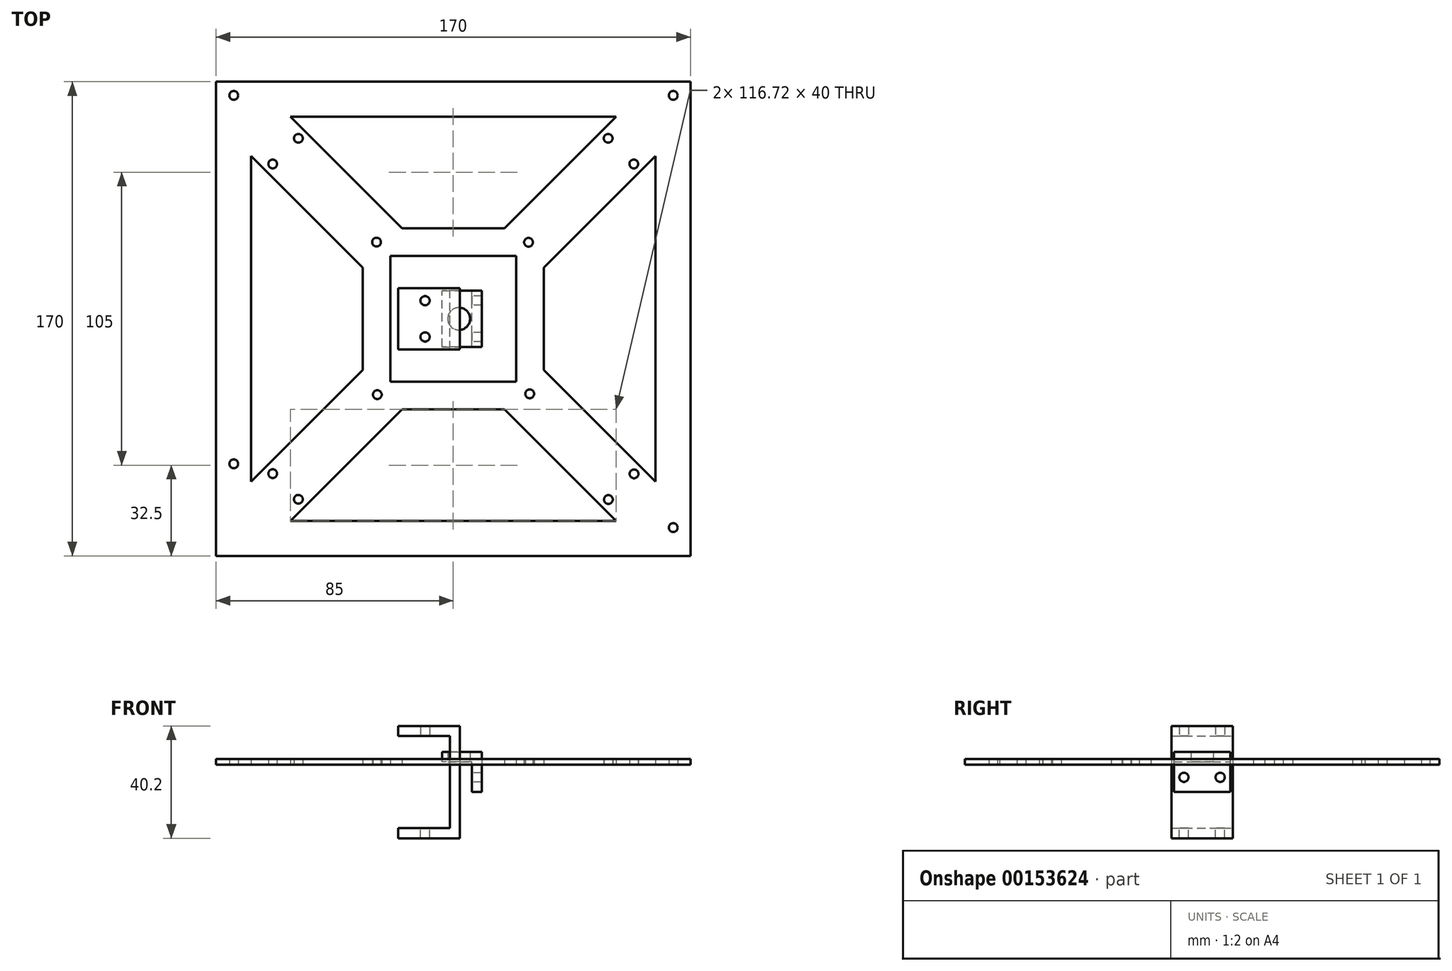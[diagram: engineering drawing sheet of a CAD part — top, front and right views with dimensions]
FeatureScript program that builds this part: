
annotation { "Feature Type Name" : "Feature", "Feature Type Description" : "" }
export const myFeature = defineFeature(function(context is Context, id is Id, definition is map)
    precondition{}
    {
        {
            var Q0;
            Q0=qCreatedBy(makeId("Front.planeOp"),FACE);
            var sketch = newSketch(context, id + "F0", { "sketchPlane" : qUnion([Q0])});
            skLineSegment(sketch, "E0", {"start": v(-19.76, 12.86) * mm, "end": v(2.4, 12.86) * mm});
            skLineSegment(sketch, "E1", {"start": v(2.4, 12.86) * mm, "end": v(2.4, -27.34) * mm});
            skLineSegment(sketch, "E2", {"start": v(2.4, -27.34) * mm, "end": v(-19.76, -27.34) * mm});
            skLineSegment(sketch, "E3", {"start": v(-19.76, -27.34) * mm, "end": v(-19.76, -23.74) * mm});
            skLineSegment(sketch, "E4", {"start": v(-19.76, -23.74) * mm, "end": v(-1.2, -23.74) * mm});
            skLineSegment(sketch, "E5", {"start": v(-1.2, -23.74) * mm, "end": v(-1.2, 9.26) * mm});
            skLineSegment(sketch, "E6", {"start": v(-1.2, 9.26) * mm, "end": v(-19.76, 9.26) * mm});
            skLineSegment(sketch, "E7", {"start": v(-19.76, 9.26) * mm, "end": v(-19.76, 12.86) * mm});
            skSolve(sketch);
        }
        {
            var Q0;
            Q0=makeQuery(id+"F0.imprint","IMPRINT",FACE,{"disambiguationData":[TD([[makeQuery(id+"F0.imprint","IMPRINT",EDGE,{"derivedFrom":sQuery(id+"F0.wireOp",EDGE,"E0")}),-1.0]])]});
            extrude(context, id + "F1", {"entities" : qUnion([Q0]), "endBound" : BoundingType.SYMMETRIC, "depth" : 22 * mm});
        }
        {
            var Q0;
            Q0=qCreatedBy(makeId("Top.planeOp"),FACE);
            var sketch = newSketch(context, id + "F2", { "sketchPlane" : qUnion([Q0])});
            skPoint(sketch, "E8", {"position": v(-10.1, 0) * mm});
            skPoint(sketch, "E9", {"position": v(-10.1, 6.5) * mm});
            skPoint(sketch, "E10", {"position": v(-10.1, -6.5) * mm});
            skSolve(sketch);
        }
        {
            var Q0;
            Q0=sQuery(id+"F2.wireOp",VERTEX,"E9");
            var Q1;
            Q1=sQuery(id+"F2.wireOp",VERTEX,"E10");
            var Q2;
            Q2=makeQuery(id+"F1.opExtrude","SWEPT_BODY",BODY,{"disambiguationData":[OSD([sQuery(id+"F0.wireOp",EDGE,"E0"),sQuery(id+"F0.wireOp",EDGE,"E1"),sQuery(id+"F0.wireOp",EDGE,"E2"),sQuery(id+"F0.wireOp",EDGE,"E3"),sQuery(id+"F0.wireOp",EDGE,"E4"),sQuery(id+"F0.wireOp",EDGE,"E5"),sQuery(id+"F0.wireOp",EDGE,"E6"),sQuery(id+"F0.wireOp",EDGE,"E7")])]});
            hole(context, id + "F3", {"style" : HoleStyle.SIMPLE, "endStyle" : HoleEndStyle.THROUGH, "standardTappedOrClearance" : lookupTablePath({ "standard" : "ISO", "fit" : "Normal", "size" : "M3", "type" : "Clearance" }), "standardBlindInLast" : lookupTablePath({ "fit" : "Standard", "standard" : "ISO", "size" : "M3", "type" : "Clearance" }), "holeDiameter" : 3.3 * mm, "locations" : qUnion([Q0, Q1]), "scope" : qUnion([Q2]), "isTappedThrough" : true});
        }
        {
            var Q0;
            Q0=sQuery(id+"F2.wireOp",VERTEX,"E10");
            var Q1;
            Q1=sQuery(id+"F2.wireOp",VERTEX,"E9");
            var Q2;
            Q2=makeQuery(id+"F1.opExtrude","SWEPT_BODY",BODY,{"disambiguationData":[OSD([sQuery(id+"F0.wireOp",EDGE,"E0"),sQuery(id+"F0.wireOp",EDGE,"E1"),sQuery(id+"F0.wireOp",EDGE,"E2"),sQuery(id+"F0.wireOp",EDGE,"E3"),sQuery(id+"F0.wireOp",EDGE,"E4"),sQuery(id+"F0.wireOp",EDGE,"E5"),sQuery(id+"F0.wireOp",EDGE,"E6"),sQuery(id+"F0.wireOp",EDGE,"E7")])]});
            hole(context, id + "F4", {"style" : HoleStyle.SIMPLE, "endStyle" : HoleEndStyle.THROUGH, "oppositeDirection" : true, "standardTappedOrClearance" : lookupTablePath({ "standard" : "ISO", "fit" : "Normal", "size" : "M3", "type" : "Clearance" }), "standardBlindInLast" : lookupTablePath({ "fit" : "Standard", "standard" : "ISO", "size" : "M3", "type" : "Clearance" }), "holeDiameter" : 3.3 * mm, "locations" : qUnion([Q0, Q1]), "scope" : qUnion([Q2]), "isTappedThrough" : true});
        }
        {
            var Q0;
            Q0=qCreatedBy(makeId("Front.planeOp"),FACE);
            var sketch = newSketch(context, id + "F5", { "sketchPlane" : qUnion([Q0])});
            skLineSegment(sketch, "E11", {"start": v(10.27, -10.7) * mm, "end": v(6.67, -10.7) * mm});
            skLineSegment(sketch, "E12", {"start": v(6.67, -10.7) * mm, "end": v(6.67, 0) * mm});
            skLineSegment(sketch, "E13", {"start": v(6.67, 0) * mm, "end": v(-4.03, 0) * mm});
            skLineSegment(sketch, "E14", {"start": v(-4.03, 0) * mm, "end": v(-4.03, 3.6) * mm});
            skLineSegment(sketch, "E15", {"start": v(-4.03, 3.6) * mm, "end": v(10.27, 3.6) * mm});
            skLineSegment(sketch, "E16", {"start": v(10.27, 3.6) * mm, "end": v(10.27, -10.7) * mm});
            skSolve(sketch);
        }
        {
            var Q0;
            Q0 = qSketchRegion(id + "F5", true);
            extrude(context, id + "F6", {"entities" : qUnion([Q0]), "endBound" : BoundingType.SYMMETRIC, "depth" : 20.2 * mm});
        }
        {
            var Q0;
            Q0=qCreatedBy(makeId("Right.planeOp"),FACE);
            var sketch = newSketch(context, id + "F7", { "sketchPlane" : qUnion([Q0])});
            skPoint(sketch, "E17", {"position": v(0, 0) * mm});
            skPoint(sketch, "E18", {"position": v(0, -5.5) * mm});
            skPoint(sketch, "E19", {"position": v(-6.5, -5.5) * mm});
            skPoint(sketch, "E20", {"position": v(6.5, -5.5) * mm});
            skSolve(sketch);
        }
        {
            var Q0;
            Q0=sQuery(id+"F7.wireOp",VERTEX,"E19");
            var Q1;
            Q1=sQuery(id+"F7.wireOp",VERTEX,"E20");
            var Q2;
            Q2=makeQuery(id+"F6.opExtrude","SWEPT_BODY",BODY,{"disambiguationData":[OSD([sQuery(id+"F5.wireOp",EDGE,"E11"),sQuery(id+"F5.wireOp",EDGE,"E12"),sQuery(id+"F5.wireOp",EDGE,"E13"),sQuery(id+"F5.wireOp",EDGE,"E14"),sQuery(id+"F5.wireOp",EDGE,"E15"),sQuery(id+"F5.wireOp",EDGE,"E16")])]});
            hole(context, id + "F8", {"style" : HoleStyle.SIMPLE, "endStyle" : HoleEndStyle.THROUGH, "oppositeDirection" : true, "standardTappedOrClearance" : lookupTablePath({ "standard" : "ISO", "fit" : "Normal", "size" : "M3", "type" : "Clearance" }), "standardBlindInLast" : lookupTablePath({ "fit" : "Standard", "standard" : "ISO", "size" : "M3", "type" : "Clearance" }), "holeDiameter" : 3.3 * mm, "locations" : qUnion([Q0, Q1]), "scope" : qUnion([Q2]), "isTappedThrough" : true});
        }
        {
            var Q0;
            Q0=qCreatedBy(makeId("Top.planeOp"),FACE);
            var sketch = newSketch(context, id + "F9", { "sketchPlane" : qUnion([Q0])});
            skPoint(sketch, "E21", {"position": v(2.02, 0) * mm});
            skSolve(sketch);
        }
        {
            var Q0;
            Q0=sQuery(id+"F9.wireOp",VERTEX,"E21");
            var Q1;
            Q1=makeQuery(id+"F6.opExtrude","SWEPT_BODY",BODY,{"disambiguationData":[OSD([sQuery(id+"F5.wireOp",EDGE,"E11"),sQuery(id+"F5.wireOp",EDGE,"E12"),sQuery(id+"F5.wireOp",EDGE,"E13"),sQuery(id+"F5.wireOp",EDGE,"E14"),sQuery(id+"F5.wireOp",EDGE,"E15"),sQuery(id+"F5.wireOp",EDGE,"E16")])]});
            hole(context, id + "F10", {"style" : HoleStyle.SIMPLE, "endStyle" : HoleEndStyle.THROUGH, "oppositeDirection" : true, "standardTappedOrClearance" : lookupTablePath({ "standard" : "ISO", "size" : "8", "type" : "Drilled" }), "standardBlindInLast" : lookupTablePath({ "standard" : "ISO", "size" : "8", "type" : "Drilled" }), "holeDiameter" : 8 * mm, "locations" : qUnion([Q0]), "scope" : qUnion([Q1]), "isTappedThrough" : true});
        }
        {
            var Q0;
            Q0=qCreatedBy(makeId("Top.planeOp"),FACE);
            var sketch = newSketch(context, id + "F11", { "sketchPlane" : qUnion([Q0])});
            skLineSegment(sketch, "E22.bottom", {"start": v(85, -85) * mm, "end": v(-85, -85) * mm});
            skLineSegment(sketch, "E22.top", {"start": v(85, 85) * mm, "end": v(-85, 85) * mm});
            skLineSegment(sketch, "E22.left", {"start": v(85, -85) * mm, "end": v(85, 85) * mm});
            skLineSegment(sketch, "E22.right", {"start": v(-85, -85) * mm, "end": v(-85, 85) * mm});
            skPoint(sketch, "E22.middle", {"position": v(0, 0) * mm});
            skLineSegment(sketch, "E23.bottom", {"start": v(72.5, -72.5) * mm, "end": v(-72.5, -72.5) * mm});
            skLineSegment(sketch, "E23.top", {"start": v(72.5, 72.5) * mm, "end": v(-72.5, 72.5) * mm});
            skLineSegment(sketch, "E23.left", {"start": v(72.5, -72.5) * mm, "end": v(72.5, 72.5) * mm});
            skLineSegment(sketch, "E23.right", {"start": v(-72.5, -72.5) * mm, "end": v(-72.5, 72.5) * mm});
            skLineSegment(sketch, "E24.bottom", {"start": v(22.5, -22.5) * mm, "end": v(-22.5, -22.5) * mm});
            skLineSegment(sketch, "E24.top", {"start": v(22.5, 22.5) * mm, "end": v(-22.5, 22.5) * mm});
            skLineSegment(sketch, "E24.left", {"start": v(22.5, -22.5) * mm, "end": v(22.5, 22.5) * mm});
            skLineSegment(sketch, "E24.right", {"start": v(-22.5, -22.5) * mm, "end": v(-22.5, 22.5) * mm});
            skLineSegment(sketch, "E25.bottom", {"start": v(32.5, -32.5) * mm, "end": v(-32.5, -32.5) * mm});
            skLineSegment(sketch, "E25.top", {"start": v(32.5, 32.5) * mm, "end": v(-32.5, 32.5) * mm});
            skLineSegment(sketch, "E25.left", {"start": v(32.5, -32.5) * mm, "end": v(32.5, 32.5) * mm});
            skLineSegment(sketch, "E25.right", {"start": v(-32.5, -32.5) * mm, "end": v(-32.5, 32.5) * mm});
            skPoint(sketch, "E26.positionSnap0", {"position": v(0, 85) * mm});
            skPoint(sketch, "E27", {"position": v(-78.65, -51.98) * mm});
            skPoint(sketch, "E28", {"position": v(78.83, -74.84) * mm});
            skPoint(sketch, "E29", {"position": v(78.83, 80.1) * mm});
            skPoint(sketch, "E30", {"position": v(-78.65, 80.1) * mm});
            skPoint(sketch, "E31", {"position": v(26.96, 27.42) * mm});
            skPoint(sketch, "E32", {"position": v(27.4, -26.9) * mm});
            skPoint(sketch, "E33", {"position": v(-27.5, 27.5) * mm});
            skPoint(sketch, "E34", {"position": v(-27.21, -27.19) * mm});
            skLineSegment(sketch, "E35", {"start": v(-72.5, 72.5) * mm, "end": v(-32.5, 32.5) * mm});
            skLineSegment(sketch, "E36", {"start": v(-60.1, 60.1) * mm, "end": v(-55.5, 64.7) * mm});
            skLineSegment(sketch, "E37", {"start": v(-60.1, 60.1) * mm, "end": v(-64.7, 55.5) * mm});
            skLineSegment(sketch, "E38.MirrorCS", {"start": v(72.5, 72.5) * mm, "end": v(32.5, 32.5) * mm});
            skLineSegment(sketch, "E39.MirrorCS", {"start": v(72.5, -72.5) * mm, "end": v(32.5, -32.5) * mm});
            skLineSegment(sketch, "E40.MirrorCS", {"start": v(-72.5, -72.5) * mm, "end": v(-32.5, -32.5) * mm});
            skPoint(sketch, "E41", {"position": v(60.1, 60.1) * mm});
            skPoint(sketch, "E42", {"position": v(60.1, -60.1) * mm});
            skPoint(sketch, "E43", {"position": v(-60.1, -60.1) * mm});
            skLineSegment(sketch, "E44", {"start": v(60.1, 60.1) * mm, "end": v(55.5, 64.7) * mm});
            skLineSegment(sketch, "E45", {"start": v(60.1, 60.1) * mm, "end": v(64.7, 55.5) * mm});
            skLineSegment(sketch, "E46", {"start": v(64.78, -55.6) * mm, "end": v(55.6, -64.79) * mm});
            skLineSegment(sketch, "E47", {"start": v(-60.1, -60.1) * mm, "end": v(-55.5, -64.7) * mm});
            skLineSegment(sketch, "E48", {"start": v(-55.5, -64.7) * mm, "end": v(-60.1, -60.1) * mm});
            skLineSegment(sketch, "E49", {"start": v(-60.1, -60.1) * mm, "end": v(-64.7, -55.5) * mm});
            skLineSegment(sketch, "E50.bottom", {"start": v(55, -55) * mm, "end": v(-55, -55) * mm});
            skLineSegment(sketch, "E50.top", {"start": v(55, 55) * mm, "end": v(-55, 55) * mm});
            skLineSegment(sketch, "E50.left", {"start": v(55, -55) * mm, "end": v(55, 55) * mm});
            skLineSegment(sketch, "E50.right", {"start": v(-55, -55) * mm, "end": v(-55, 55) * mm});
            skLineSegment(sketch, "E51", {"start": v(-22.5, -8.36) * mm, "end": v(-85, -70.86) * mm});
            skLineSegment(sketch, "E52.MirrorCS", {"start": v(-8.36, -22.5) * mm, "end": v(-70.86, -85) * mm});
            skLineSegment(sketch, "E53.MirrorCS", {"start": v(22.5, -8.36) * mm, "end": v(85, -70.86) * mm});
            skLineSegment(sketch, "E54.MirrorCS", {"start": v(8.36, -22.5) * mm, "end": v(70.86, -85) * mm});
            skLineSegment(sketch, "E55.MirrorCS", {"start": v(22.5, 8.36) * mm, "end": v(85, 70.86) * mm});
            skLineSegment(sketch, "E56.MirrorCS", {"start": v(8.36, 22.5) * mm, "end": v(70.86, 85) * mm});
            skLineSegment(sketch, "E57.MirrorCS", {"start": v(-8.36, 22.5) * mm, "end": v(-70.86, 85) * mm});
            skLineSegment(sketch, "E58.MirrorCS", {"start": v(-22.5, 8.36) * mm, "end": v(-85, 70.86) * mm});
            skSolve(sketch);
        }
        {
            var Q0;
            {var subQ1=sQuery(id+"F11.wireOp",EDGE,"E25.right");var subQ3=sQuery(id+"F11.wireOp",EDGE,"E58.MirrorCS");var subQ4=makeQuery(id+"F11.imprint","INTERSECT",VERTEX,{"derivedFrom":[subQ1,subQ3]});Q0=makeQuery(id+"F11.imprint","IMPRINT",FACE,{"disambiguationData":[TD([[makeQuery(id+"F11.imprint","IMPRINT",EDGE,{"disambiguationData":[TD([[subQ4,-1.0]])],"derivedFrom":subQ3}),-1.0]])]});}
            var Q1;
            {var subQ1=sQuery(id+"F11.wireOp",EDGE,"E25.top");var subQ3=sQuery(id+"F11.wireOp",EDGE,"E57.MirrorCS");var subQ4=makeQuery(id+"F11.imprint","INTERSECT",VERTEX,{"derivedFrom":[subQ1,subQ3]});Q1=makeQuery(id+"F11.imprint","IMPRINT",FACE,{"disambiguationData":[TD([[makeQuery(id+"F11.imprint","IMPRINT",EDGE,{"disambiguationData":[TD([[subQ4,-1.0]])],"derivedFrom":subQ3}),1.0]])]});}
            var Q2;
            {var subQ1=sQuery(id+"F11.wireOp",EDGE,"E35");var subQ7=makeQuery(id+"F11.imprint","IMPRINT",VERTEX,{"derivedFrom":subQ1});Q2=makeQuery(id+"F11.imprint","IMPRINT",FACE,{"disambiguationData":[TD([[makeQuery(id+"F11.imprint","IMPRINT",EDGE,{"disambiguationData":[TD([[subQ7,1.0]])],"derivedFrom":subQ1}),1.0]])]});}
            var Q3;
            {var subQ1=sQuery(id+"F11.wireOp",EDGE,"E35");var subQ5=makeQuery(id+"F11.imprint","IMPRINT",VERTEX,{"derivedFrom":subQ1});Q3=makeQuery(id+"F11.imprint","IMPRINT",FACE,{"disambiguationData":[TD([[makeQuery(id+"F11.imprint","IMPRINT",EDGE,{"disambiguationData":[TD([[subQ5,1.0]])],"derivedFrom":subQ1}),-1.0]])]});}
            var Q4;
            {var subQ0=sQuery(id+"F11.wireOp",EDGE,"E56.MirrorCS");var subQ1=sQuery(id+"F11.wireOp",EDGE,"E22.top");var subQ2=makeQuery(id+"F11.imprint","INTERSECT",VERTEX,{"derivedFrom":[subQ1,subQ0]});Q4=makeQuery(id+"F11.imprint","IMPRINT",FACE,{"disambiguationData":[TD([[makeQuery(id+"F11.imprint","IMPRINT",EDGE,{"disambiguationData":[TD([[subQ2,-1.0]])],"derivedFrom":subQ1}),1.0]])]});}
            var Q5;
            {var subQ5=sQuery(id+"F11.wireOp",EDGE,"E22.right");var subQ9=sQuery(id+"F11.wireOp",EDGE,"E22.top");var subQ10=makeQuery(id+"F11.imprint","INTERSECT",VERTEX,{"derivedFrom":[subQ9,subQ5]});Q5=makeQuery(id+"F11.imprint","IMPRINT",FACE,{"disambiguationData":[TD([[makeQuery(id+"F11.imprint","IMPRINT",EDGE,{"disambiguationData":[TD([[subQ10,1.0]])],"derivedFrom":subQ9}),1.0]])]});}
            var Q6;
            {var subQ0=sQuery(id+"F11.wireOp",EDGE,"E51");var subQ1=sQuery(id+"F11.wireOp",EDGE,"E22.right");var subQ2=makeQuery(id+"F11.imprint","INTERSECT",VERTEX,{"derivedFrom":[subQ1,subQ0]});Q6=makeQuery(id+"F11.imprint","IMPRINT",FACE,{"disambiguationData":[TD([[makeQuery(id+"F11.imprint","IMPRINT",EDGE,{"disambiguationData":[TD([[subQ2,-1.0]])],"derivedFrom":subQ1}),-1.0]])]});}
            var Q7;
            {var subQ1=sQuery(id+"F11.wireOp",EDGE,"E25.right");var subQ3=sQuery(id+"F11.wireOp",EDGE,"E51");var subQ4=makeQuery(id+"F11.imprint","INTERSECT",VERTEX,{"derivedFrom":[subQ1,subQ3]});Q7=makeQuery(id+"F11.imprint","IMPRINT",FACE,{"disambiguationData":[TD([[makeQuery(id+"F11.imprint","IMPRINT",EDGE,{"disambiguationData":[TD([[subQ4,-1.0]])],"derivedFrom":subQ3}),1.0]])]});}
            var Q8;
            {var subQ1=sQuery(id+"F11.wireOp",EDGE,"E40.MirrorCS");var subQ5=makeQuery(id+"F11.imprint","IMPRINT",VERTEX,{"derivedFrom":subQ1});Q8=makeQuery(id+"F11.imprint","IMPRINT",FACE,{"disambiguationData":[TD([[makeQuery(id+"F11.imprint","IMPRINT",EDGE,{"disambiguationData":[TD([[subQ5,1.0]])],"derivedFrom":subQ1}),1.0]])]});}
            var Q9;
            {var subQ7=sQuery(id+"F11.wireOp",EDGE,"E22.right");var subQ8=sQuery(id+"F11.wireOp",EDGE,"E22.bottom");var subQ9=makeQuery(id+"F11.imprint","INTERSECT",VERTEX,{"derivedFrom":[subQ8,subQ7]});Q9=makeQuery(id+"F11.imprint","IMPRINT",FACE,{"disambiguationData":[TD([[makeQuery(id+"F11.imprint","IMPRINT",EDGE,{"disambiguationData":[TD([[subQ9,1.0]])],"derivedFrom":subQ8}),-1.0]])]});}
            var Q10;
            {var subQ1=sQuery(id+"F11.wireOp",EDGE,"E25.bottom");var subQ3=sQuery(id+"F11.wireOp",EDGE,"E52.MirrorCS");var subQ4=makeQuery(id+"F11.imprint","INTERSECT",VERTEX,{"derivedFrom":[subQ1,subQ3]});Q10=makeQuery(id+"F11.imprint","IMPRINT",FACE,{"disambiguationData":[TD([[makeQuery(id+"F11.imprint","IMPRINT",EDGE,{"disambiguationData":[TD([[subQ4,-1.0]])],"derivedFrom":subQ3}),-1.0]])]});}
            var Q11;
            {var subQ7=sQuery(id+"F11.wireOp",EDGE,"E24.right");var subQ8=sQuery(id+"F11.wireOp",EDGE,"E24.bottom");var subQ9=makeQuery(id+"F11.imprint","INTERSECT",VERTEX,{"derivedFrom":[subQ8,subQ7]});Q11=makeQuery(id+"F11.imprint","IMPRINT",FACE,{"disambiguationData":[TD([[makeQuery(id+"F11.imprint","IMPRINT",EDGE,{"disambiguationData":[TD([[subQ9,1.0]])],"derivedFrom":subQ8}),1.0]])]});}
            var Q12;
            {var subQ0=sQuery(id+"F11.wireOp",EDGE,"E51");var subQ1=sQuery(id+"F11.wireOp",EDGE,"E24.right");var subQ2=makeQuery(id+"F11.imprint","INTERSECT",VERTEX,{"derivedFrom":[subQ1,subQ0]});Q12=makeQuery(id+"F11.imprint","IMPRINT",FACE,{"disambiguationData":[TD([[makeQuery(id+"F11.imprint","IMPRINT",EDGE,{"disambiguationData":[TD([[subQ2,-1.0]])],"derivedFrom":subQ1}),1.0]])]});}
            var Q13;
            {var subQ7=sQuery(id+"F11.wireOp",EDGE,"E24.right");var subQ8=sQuery(id+"F11.wireOp",EDGE,"E24.top");var subQ9=makeQuery(id+"F11.imprint","INTERSECT",VERTEX,{"derivedFrom":[subQ8,subQ7]});Q13=makeQuery(id+"F11.imprint","IMPRINT",FACE,{"disambiguationData":[TD([[makeQuery(id+"F11.imprint","IMPRINT",EDGE,{"disambiguationData":[TD([[subQ9,1.0]])],"derivedFrom":subQ8}),-1.0]])]});}
            var Q14;
            {var subQ0=sQuery(id+"F11.wireOp",EDGE,"E56.MirrorCS");var subQ1=sQuery(id+"F11.wireOp",EDGE,"E24.top");var subQ2=makeQuery(id+"F11.imprint","INTERSECT",VERTEX,{"derivedFrom":[subQ1,subQ0]});Q14=makeQuery(id+"F11.imprint","IMPRINT",FACE,{"disambiguationData":[TD([[makeQuery(id+"F11.imprint","IMPRINT",EDGE,{"disambiguationData":[TD([[subQ2,-1.0]])],"derivedFrom":subQ1}),-1.0]])]});}
            var Q15;
            {var subQ5=sQuery(id+"F11.wireOp",EDGE,"E24.left");var subQ6=sQuery(id+"F11.wireOp",EDGE,"E24.top");var subQ7=makeQuery(id+"F11.imprint","INTERSECT",VERTEX,{"derivedFrom":[subQ6,subQ5]});Q15=makeQuery(id+"F11.imprint","IMPRINT",FACE,{"disambiguationData":[TD([[makeQuery(id+"F11.imprint","IMPRINT",EDGE,{"disambiguationData":[TD([[subQ7,-1.0]])],"derivedFrom":subQ6}),-1.0]])]});}
            var Q16;
            {var subQ1=sQuery(id+"F11.wireOp",EDGE,"E25.top");var subQ3=sQuery(id+"F11.wireOp",EDGE,"E56.MirrorCS");var subQ4=makeQuery(id+"F11.imprint","INTERSECT",VERTEX,{"derivedFrom":[subQ1,subQ3]});Q16=makeQuery(id+"F11.imprint","IMPRINT",FACE,{"disambiguationData":[TD([[makeQuery(id+"F11.imprint","IMPRINT",EDGE,{"disambiguationData":[TD([[subQ4,-1.0]])],"derivedFrom":subQ3}),-1.0]])]});}
            var Q17;
            {var subQ1=sQuery(id+"F11.wireOp",EDGE,"E25.left");var subQ3=sQuery(id+"F11.wireOp",EDGE,"E55.MirrorCS");var subQ4=makeQuery(id+"F11.imprint","INTERSECT",VERTEX,{"derivedFrom":[subQ1,subQ3]});Q17=makeQuery(id+"F11.imprint","IMPRINT",FACE,{"disambiguationData":[TD([[makeQuery(id+"F11.imprint","IMPRINT",EDGE,{"disambiguationData":[TD([[subQ4,-1.0]])],"derivedFrom":subQ3}),1.0]])]});}
            var Q18;
            {var subQ1=sQuery(id+"F11.wireOp",EDGE,"E38.MirrorCS");var subQ7=makeQuery(id+"F11.imprint","IMPRINT",VERTEX,{"derivedFrom":subQ1});Q18=makeQuery(id+"F11.imprint","IMPRINT",FACE,{"disambiguationData":[TD([[makeQuery(id+"F11.imprint","IMPRINT",EDGE,{"disambiguationData":[TD([[subQ7,1.0]])],"derivedFrom":subQ1}),1.0]])]});}
            var Q19;
            {var subQ0=sQuery(id+"F11.wireOp",EDGE,"E38.MirrorCS");var subQ1=makeQuery(id+"F11.imprint","IMPRINT",VERTEX,{"derivedFrom":subQ0});Q19=makeQuery(id+"F11.imprint","IMPRINT",FACE,{"disambiguationData":[TD([[makeQuery(id+"F11.imprint","IMPRINT",EDGE,{"disambiguationData":[TD([[subQ1,1.0]])],"derivedFrom":subQ0}),-1.0]])]});}
            var Q20;
            {var subQ5=sQuery(id+"F11.wireOp",EDGE,"E22.left");var subQ6=sQuery(id+"F11.wireOp",EDGE,"E22.top");var subQ7=makeQuery(id+"F11.imprint","INTERSECT",VERTEX,{"derivedFrom":[subQ6,subQ5]});Q20=makeQuery(id+"F11.imprint","IMPRINT",FACE,{"disambiguationData":[TD([[makeQuery(id+"F11.imprint","IMPRINT",EDGE,{"disambiguationData":[TD([[subQ7,-1.0]])],"derivedFrom":subQ6}),1.0]])]});}
            var Q21;
            {var subQ0=sQuery(id+"F11.wireOp",EDGE,"E53.MirrorCS");var subQ1=sQuery(id+"F11.wireOp",EDGE,"E22.left");var subQ2=makeQuery(id+"F11.imprint","INTERSECT",VERTEX,{"derivedFrom":[subQ1,subQ0]});Q21=makeQuery(id+"F11.imprint","IMPRINT",FACE,{"disambiguationData":[TD([[makeQuery(id+"F11.imprint","IMPRINT",EDGE,{"disambiguationData":[TD([[subQ2,-1.0]])],"derivedFrom":subQ1}),1.0]])]});}
            var Q22;
            {var subQ7=sQuery(id+"F11.wireOp",EDGE,"E22.left");var subQ8=sQuery(id+"F11.wireOp",EDGE,"E22.bottom");var subQ9=makeQuery(id+"F11.imprint","INTERSECT",VERTEX,{"derivedFrom":[subQ8,subQ7]});Q22=makeQuery(id+"F11.imprint","IMPRINT",FACE,{"disambiguationData":[TD([[makeQuery(id+"F11.imprint","IMPRINT",EDGE,{"disambiguationData":[TD([[subQ9,-1.0]])],"derivedFrom":subQ8}),-1.0]])]});}
            var Q23;
            {var subQ1=sQuery(id+"F11.wireOp",EDGE,"E39.MirrorCS");var subQ7=makeQuery(id+"F11.imprint","IMPRINT",VERTEX,{"derivedFrom":subQ1});Q23=makeQuery(id+"F11.imprint","IMPRINT",FACE,{"disambiguationData":[TD([[makeQuery(id+"F11.imprint","IMPRINT",EDGE,{"disambiguationData":[TD([[subQ7,1.0]])],"derivedFrom":subQ1}),1.0]])]});}
            var Q24;
            {var subQ1=sQuery(id+"F11.wireOp",EDGE,"E25.bottom");var subQ3=sQuery(id+"F11.wireOp",EDGE,"E54.MirrorCS");var subQ4=makeQuery(id+"F11.imprint","INTERSECT",VERTEX,{"derivedFrom":[subQ1,subQ3]});Q24=makeQuery(id+"F11.imprint","IMPRINT",FACE,{"disambiguationData":[TD([[makeQuery(id+"F11.imprint","IMPRINT",EDGE,{"disambiguationData":[TD([[subQ4,-1.0]])],"derivedFrom":subQ3}),1.0]])]});}
            var Q25;
            {var subQ1=sQuery(id+"F11.wireOp",EDGE,"E25.left");var subQ3=sQuery(id+"F11.wireOp",EDGE,"E53.MirrorCS");var subQ4=makeQuery(id+"F11.imprint","INTERSECT",VERTEX,{"derivedFrom":[subQ1,subQ3]});Q25=makeQuery(id+"F11.imprint","IMPRINT",FACE,{"disambiguationData":[TD([[makeQuery(id+"F11.imprint","IMPRINT",EDGE,{"disambiguationData":[TD([[subQ4,-1.0]])],"derivedFrom":subQ3}),-1.0]])]});}
            var Q26;
            {var subQ1=sQuery(id+"F11.wireOp",EDGE,"E39.MirrorCS");var subQ5=makeQuery(id+"F11.imprint","IMPRINT",VERTEX,{"derivedFrom":subQ1});Q26=makeQuery(id+"F11.imprint","IMPRINT",FACE,{"disambiguationData":[TD([[makeQuery(id+"F11.imprint","IMPRINT",EDGE,{"disambiguationData":[TD([[subQ5,1.0]])],"derivedFrom":subQ1}),-1.0]])]});}
            var Q27;
            {var subQ7=sQuery(id+"F11.wireOp",EDGE,"E24.left");var subQ8=sQuery(id+"F11.wireOp",EDGE,"E24.bottom");var subQ9=makeQuery(id+"F11.imprint","INTERSECT",VERTEX,{"derivedFrom":[subQ8,subQ7]});Q27=makeQuery(id+"F11.imprint","IMPRINT",FACE,{"disambiguationData":[TD([[makeQuery(id+"F11.imprint","IMPRINT",EDGE,{"disambiguationData":[TD([[subQ9,-1.0]])],"derivedFrom":subQ8}),1.0]])]});}
            var Q28;
            {var subQ0=sQuery(id+"F11.wireOp",EDGE,"E53.MirrorCS");var subQ1=sQuery(id+"F11.wireOp",EDGE,"E24.left");var subQ2=makeQuery(id+"F11.imprint","INTERSECT",VERTEX,{"derivedFrom":[subQ1,subQ0]});Q28=makeQuery(id+"F11.imprint","IMPRINT",FACE,{"disambiguationData":[TD([[makeQuery(id+"F11.imprint","IMPRINT",EDGE,{"disambiguationData":[TD([[subQ2,-1.0]])],"derivedFrom":subQ1}),-1.0]])]});}
            var Q29;
            {var subQ0=sQuery(id+"F11.wireOp",EDGE,"E52.MirrorCS");var subQ1=sQuery(id+"F11.wireOp",EDGE,"E24.bottom");var subQ2=makeQuery(id+"F11.imprint","INTERSECT",VERTEX,{"derivedFrom":[subQ1,subQ0]});Q29=makeQuery(id+"F11.imprint","IMPRINT",FACE,{"disambiguationData":[TD([[makeQuery(id+"F11.imprint","IMPRINT",EDGE,{"disambiguationData":[TD([[subQ2,1.0]])],"derivedFrom":subQ1}),1.0]])]});}
            var Q30;
            {var subQ1=sQuery(id+"F11.wireOp",EDGE,"E40.MirrorCS");var subQ5=makeQuery(id+"F11.imprint","IMPRINT",VERTEX,{"derivedFrom":subQ1});Q30=makeQuery(id+"F11.imprint","IMPRINT",FACE,{"disambiguationData":[TD([[makeQuery(id+"F11.imprint","IMPRINT",EDGE,{"disambiguationData":[TD([[subQ5,1.0]])],"derivedFrom":subQ1}),-1.0]])]});}
            var Q31;
            {var subQ0=sQuery(id+"F11.wireOp",EDGE,"E52.MirrorCS");var subQ1=sQuery(id+"F11.wireOp",EDGE,"E22.bottom");var subQ2=makeQuery(id+"F11.imprint","INTERSECT",VERTEX,{"derivedFrom":[subQ1,subQ0]});Q31=makeQuery(id+"F11.imprint","IMPRINT",FACE,{"disambiguationData":[TD([[makeQuery(id+"F11.imprint","IMPRINT",EDGE,{"disambiguationData":[TD([[subQ2,1.0]])],"derivedFrom":subQ1}),-1.0]])]});}
            extrude(context, id + "F12", {"entities" : qUnion([Q0, Q1, Q2, Q3, Q4, Q5, Q6, Q7, Q8, Q9, Q10, Q11, Q12, Q13, Q14, Q15, Q16, Q17, Q18, Q19, Q20, Q21, Q22, Q23, Q24, Q25, Q26, Q27, Q28, Q29, Q30, Q31]), "endBound" : BoundingType.SYMMETRIC, "depth" : 2 * mm});
        }
        {
            var Q0;
            Q0=sQuery(id+"F11.wireOp",VERTEX,"E30");
            var Q1;
            Q1=sQuery(id+"F11.wireOp",VERTEX,"E36.end");
            var Q2;
            Q2=sQuery(id+"F11.wireOp",VERTEX,"E44.end");
            var Q3;
            Q3=sQuery(id+"F11.wireOp",VERTEX,"E45.end");
            var Q4;
            Q4=sQuery(id+"F11.wireOp",VERTEX,"E29");
            var Q5;
            Q5=sQuery(id+"F11.wireOp",VERTEX,"E37.end");
            var Q6;
            Q6=sQuery(id+"F11.wireOp",VERTEX,"E33");
            var Q7;
            Q7=sQuery(id+"F11.wireOp",VERTEX,"E31");
            var Q8;
            Q8=sQuery(id+"F11.wireOp",VERTEX,"E32");
            var Q9;
            Q9=sQuery(id+"F11.wireOp",VERTEX,"E34");
            var Q10;
            Q10=sQuery(id+"F11.wireOp",VERTEX,"E49.end");
            var Q11;
            Q11=sQuery(id+"F11.wireOp",VERTEX,"E47.end");
            var Q12;
            Q12=sQuery(id+"F11.wireOp",VERTEX,"E27");
            var Q13;
            Q13=sQuery(id+"F11.wireOp",VERTEX,"E46.end");
            var Q14;
            Q14=sQuery(id+"F11.wireOp",VERTEX,"E46.start");
            var Q15;
            Q15=sQuery(id+"F11.wireOp",VERTEX,"E28");
            var Q16;
            Q16=makeQuery(id+"F12.opExtrude","SWEPT_BODY",BODY,{"disambiguationData":[OSD([sQuery(id+"F11.wireOp",EDGE,"E22.bottom"),sQuery(id+"F11.wireOp",EDGE,"E22.top"),sQuery(id+"F11.wireOp",EDGE,"E22.left"),sQuery(id+"F11.wireOp",EDGE,"E22.right"),sQuery(id+"F11.wireOp",EDGE,"E23.bottom"),sQuery(id+"F11.wireOp",EDGE,"E23.top"),sQuery(id+"F11.wireOp",EDGE,"E23.left"),sQuery(id+"F11.wireOp",EDGE,"E23.right"),sQuery(id+"F11.wireOp",EDGE,"E24.bottom"),sQuery(id+"F11.wireOp",EDGE,"E24.top"),sQuery(id+"F11.wireOp",EDGE,"E24.left"),sQuery(id+"F11.wireOp",EDGE,"E24.right"),sQuery(id+"F11.wireOp",EDGE,"E25.bottom"),sQuery(id+"F11.wireOp",EDGE,"E25.top"),sQuery(id+"F11.wireOp",EDGE,"E25.left"),sQuery(id+"F11.wireOp",EDGE,"E25.right"),sQuery(id+"F11.wireOp",EDGE,"E51"),sQuery(id+"F11.wireOp",EDGE,"E52.MirrorCS"),sQuery(id+"F11.wireOp",EDGE,"E53.MirrorCS"),sQuery(id+"F11.wireOp",EDGE,"E54.MirrorCS"),sQuery(id+"F11.wireOp",EDGE,"E55.MirrorCS"),sQuery(id+"F11.wireOp",EDGE,"E56.MirrorCS"),sQuery(id+"F11.wireOp",EDGE,"E57.MirrorCS"),sQuery(id+"F11.wireOp",EDGE,"E58.MirrorCS")])]});
            hole(context, id + "F13", {"style" : HoleStyle.SIMPLE, "endStyle" : HoleEndStyle.THROUGH, "oppositeDirection" : true, "standardTappedOrClearance" : lookupTablePath({ "standard" : "ISO", "fit" : "Close", "size" : "M3", "type" : "Clearance" }), "standardBlindInLast" : lookupTablePath({ "fit" : "Close", "standard" : "ISO", "size" : "M3", "type" : "Clearance" }), "holeDiameter" : 3.15 * mm, "locations" : qUnion([Q0, Q1, Q2, Q3, Q4, Q5, Q6, Q7, Q8, Q9, Q10, Q11, Q12, Q13, Q14, Q15]), "scope" : qUnion([Q16]), "isTappedThrough" : true});
        }
        {
            var Q0;
            Q0=sQuery(id+"F11.wireOp",VERTEX,"E31");
            var Q1;
            Q1=sQuery(id+"F11.wireOp",VERTEX,"E33");
            var Q2;
            Q2=sQuery(id+"F11.wireOp",VERTEX,"E37.end");
            var Q3;
            Q3=sQuery(id+"F11.wireOp",VERTEX,"E36.end");
            var Q4;
            Q4=sQuery(id+"F11.wireOp",VERTEX,"E30");
            var Q5;
            Q5=sQuery(id+"F11.wireOp",VERTEX,"E45.end");
            var Q6;
            Q6=sQuery(id+"F11.wireOp",VERTEX,"E44.end");
            var Q7;
            Q7=sQuery(id+"F11.wireOp",VERTEX,"E29");
            var Q8;
            Q8=sQuery(id+"F11.wireOp",VERTEX,"E28");
            var Q9;
            Q9=sQuery(id+"F11.wireOp",VERTEX,"E46.start");
            var Q10;
            Q10=sQuery(id+"F11.wireOp",VERTEX,"E46.end");
            var Q11;
            Q11=sQuery(id+"F11.wireOp",VERTEX,"E32");
            var Q12;
            Q12=sQuery(id+"F11.wireOp",VERTEX,"E34");
            var Q13;
            Q13=sQuery(id+"F11.wireOp",VERTEX,"E27");
            var Q14;
            Q14=sQuery(id+"F11.wireOp",VERTEX,"E49.end");
            var Q15;
            Q15=sQuery(id+"F11.wireOp",VERTEX,"E47.end");
            var Q16;
            Q16=makeQuery(id+"F12.opExtrude","SWEPT_BODY",BODY,{"disambiguationData":[OSD([sQuery(id+"F11.wireOp",EDGE,"E22.bottom"),sQuery(id+"F11.wireOp",EDGE,"E22.top"),sQuery(id+"F11.wireOp",EDGE,"E22.left"),sQuery(id+"F11.wireOp",EDGE,"E22.right"),sQuery(id+"F11.wireOp",EDGE,"E23.bottom"),sQuery(id+"F11.wireOp",EDGE,"E23.top"),sQuery(id+"F11.wireOp",EDGE,"E23.left"),sQuery(id+"F11.wireOp",EDGE,"E23.right"),sQuery(id+"F11.wireOp",EDGE,"E24.bottom"),sQuery(id+"F11.wireOp",EDGE,"E24.top"),sQuery(id+"F11.wireOp",EDGE,"E24.left"),sQuery(id+"F11.wireOp",EDGE,"E24.right"),sQuery(id+"F11.wireOp",EDGE,"E25.bottom"),sQuery(id+"F11.wireOp",EDGE,"E25.top"),sQuery(id+"F11.wireOp",EDGE,"E25.left"),sQuery(id+"F11.wireOp",EDGE,"E25.right"),sQuery(id+"F11.wireOp",EDGE,"E51"),sQuery(id+"F11.wireOp",EDGE,"E52.MirrorCS"),sQuery(id+"F11.wireOp",EDGE,"E53.MirrorCS"),sQuery(id+"F11.wireOp",EDGE,"E54.MirrorCS"),sQuery(id+"F11.wireOp",EDGE,"E55.MirrorCS"),sQuery(id+"F11.wireOp",EDGE,"E56.MirrorCS"),sQuery(id+"F11.wireOp",EDGE,"E57.MirrorCS"),sQuery(id+"F11.wireOp",EDGE,"E58.MirrorCS")])]});
            hole(context, id + "F14", {"style" : HoleStyle.SIMPLE, "endStyle" : HoleEndStyle.THROUGH, "standardTappedOrClearance" : lookupTablePath({ "standard" : "ISO", "fit" : "Close", "size" : "M3", "type" : "Clearance" }), "standardBlindInLast" : lookupTablePath({ "fit" : "Close", "standard" : "ISO", "size" : "M3", "type" : "Clearance" }), "holeDiameter" : 3.15 * mm, "locations" : qUnion([Q0, Q1, Q2, Q3, Q4, Q5, Q6, Q7, Q8, Q9, Q10, Q11, Q12, Q13, Q14, Q15]), "scope" : qUnion([Q16]), "isTappedThrough" : true});
        }
    });
